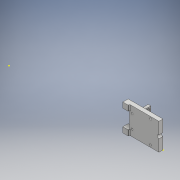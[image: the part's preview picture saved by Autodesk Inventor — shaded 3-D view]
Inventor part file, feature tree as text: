
AUTODESK INVENTOR PART (.ipt)
format: ipt  version: 2018 (Build 220112000, 112)  size: 628,224 bytes
history: native  units: mm
features: sketch x33, extrude x25, fillet x8, hole x6
ambient origin geometry x8: Origin, YZ Plane, XZ Plane, XY Plane, X Axis, Y Axis, Z Axis, Center Point
bodies: Solid1 (feature_tree)
feature tree (72):
  extrude  "Extrusion1"  Depth=50.0mm
  hole  "Hole1"  [1 undecoded]
  hole  "Hole2"  [1 undecoded]
  extrude  "Extrusion2"  Depth=25.0mm
  extrude  "Extrusion3"  Depth=25.0mm
  extrude  "Extrusion4"  Depth=5.0mm
  sketch  "Sketch7"  dims[d25=10.0mm d26=5.0mm]
  extrude  "Extrusion5"  Depth=5.0mm
  extrude  "Extrusion6"  Depth=17.5mm
  extrude  "Extrusion7"  Depth=35.0mm
  extrude  "Extrusion8"  Depth=35.0mm
  extrude  "Extrusion9"  Depth=2.0mm TaperAngle=0.0deg
  extrude  "Extrusion10"  Depth=7.5mm TaperAngle=0.0deg
  extrude  "Extrusion11"  Depth=10.0mm
  extrude  "Extrusion12"  Depth=7.5mm
  fillet  "Fillet1"  Radius=7.5mm
  fillet  "Fillet2"  Radius=25.0mm
  fillet  "Fillet3"  Radius=3.0mm
  fillet  "Fillet4"  Radius=3.2mm
  fillet  "Fillet5"  Radius=2.1mm
  fillet  "Fillet6"  Radius=5.5mm
  extrude  "Extrusion13"  Depth=92.5mm TaperAngle=0.0deg
  sketch  "Sketch17"  dims[d58=4.25mm d59=241.0mm d60=0.0mm]
  hole  "Hole3"  [1 undecoded]
  hole  "Hole4"  [1 undecoded]
  extrude  "Extrusion14"  Depth=5.0mm
  extrude  "Extrusion15"  Depth=2.5mm TaperAngle=0.0deg
  extrude  "Extrusion16"  Depth=30.0mm
  extrude  "Extrusion17"  Depth=2.5mm
  extrude  "Extrusion18"  Depth=14.55mm TaperAngle=0.0deg
  extrude  "Extrusion19"  Depth=0.1mm
  extrude  "Extrusion20"  Depth=3.25mm
  extrude  "Extrusion21"  Depth=3.25mm
  hole  "Hole5"  [1 undecoded]
  extrude  "Extrusion22"  Depth=2.0mm
  extrude  "Extrusion23"  Depth=15.0mm
  extrude  "Extrusion24"  Depth=10.0mm TaperAngle=0.0deg
  extrude  "Extrusion25"  Depth=2.0mm
  fillet  "Fillet7"  Radius=100.0mm
  fillet  "Fillet8"  Radius=100.0mm
  hole  "Hole6"  [1 undecoded]
  sketch  "Sketch1"  dims[d0=50.0mm d1=50.0mm]
  sketch  "Sketch2"  dims[d2=240.0mm d3=7.5mm]
  sketch  "Sketch3"  dims[d4=7.5mm d5=7.5mm d6=0.0mm]
  sketch  "Sketch4"  dims[d7=6.35mm d8=6.0mm d9=4.0mm d10=2.0mm d11=90.0deg d12=8.0mm d13=20.594885mm d14=25.0mm]
  sketch  "Sketch5"  dims[d15=3.3mm d16=6.0mm d17=4.0mm d18=2.0mm d19=90.0deg d20=8.0mm d21=20.594885mm d22=25.0mm]
  sketch  "Sketch6"  dims[d23=180.0deg d24=5.0mm]
  sketch  "Sketch8"  dims[d27=17.5mm d28=0.0mm d30=35.0mm]
  sketch  "Sketch9"  dims[d31=35.0mm d32=35.0mm]
  sketch  "Sketch10"  dims[d33=35.0mm d34=35.0mm]
  sketch  "Sketch11"  dims[d35=35.0mm d36=2.0mm d37=0.0mm]
  sketch  "Sketch12"  dims[d38=10.0mm d39=7.5mm d40=0.0mm]
  sketch  "Sketch13"  dims[d41=100.0mm d42=10.0mm]
  sketch  "Sketch14"  dims[d43=7.5mm d44=0.0mm d45=7.5mm d46=7.5mm d47=25.0mm d48=0.0mm d49=3.0mm d50=3.2mm d51=2.1mm d52=5.5mm]
  sketch  "Sketch15"  dims[d53=3.3mm d54=92.5mm d55=0.0mm]
  sketch  "Sketch16"  dims[d56=5.5mm d57=3.3mm]
  sketch  "Sketch18"  dims[d61=4.44mm d62=5.0mm]
  sketch  "Sketch19"  dims[d63=2.5mm d64=91.25mm d65=0.0mm]
  sketch  "Sketch20"  dims[d66=30.0mm d67=6.35mm]
  sketch  "Sketch21"  dims[d68=3.8mm d69=0.0mm d70=2.5mm]
  sketch  "Sketch22"  dims[d71=14.55mm d72=0.0mm d73=14.55mm d74=0.0mm]
  sketch  "Sketch23"  dims[d75=0.1mm d76=0.1mm]
  sketch  "Sketch24"  dims[d77=3.25mm d78=3.25mm]
  sketch  "Sketch25"  dims[d79=3.25mm d80=3.25mm]
  sketch  "Sketch26"  dims[d81=35.0mm d82=10.0mm]
  sketch  "Sketch27"  dims[d83=2.0mm d84=0.0mm d85=3.6mm]
  sketch  "Sketch28"  dims[d86=3.6mm]
  sketch  "Sketch29"  dims[d87=3.3mm d88=6.0mm d89=4.0mm d90=2.0mm d91=90.0deg d92=15.0mm d93=20.594885mm]
  sketch  "Sketch30"  dims[d94=3.3mm d95=6.0mm d96=4.0mm d97=2.0mm d98=90.0deg d99=15.0mm d100=20.594885mm d101=6.0mm]
  sketch  "Sketch31"  dims[d102=20.0mm d103=0.0mm d104=10.0mm d105=0.0mm]
  sketch  "Sketch32"  dims[d106=2.0mm d107=0.0mm d108=4.0mm d109=100.0mm d110=0.0mm d111=100.0mm d112=0.0mm]
  sketch  "Sketch33"  dims[d113=5.0mm d114=2.0mm d115=0.0mm d116=3.3mm d117=3.3mm d118=3.3mm d119=3.3mm d120=2.0mm d121=0.0mm d122=5.5mm d123=0.0mm d124=3.3mm d125=6.0mm d126=4.0mm d127=2.0mm d128=90.0deg d129=8.0mm d130=20.594885mm d131=42.0mm d132=17.0mm d133=21.0mm d135=8.5mm d136=15.825mm d137=3.5mm d138=21.0mm d139=3.3mm d140=3.3mm d141=3.3mm d142=10.0mm d143=0.0mm d144=7.5mm d145=0.0mm d146=100.0mm d147=0.0mm d148=10.0mm d149=10.0mm d150=10.0mm d151=10.0mm d152=10.0mm d153=0.0mm d154=2.0mm d155=2.0mm d156=6.25mm d157=6.0mm d158=4.0mm d159=2.0mm d160=90.0deg d161=8.0mm d162=0.0mm]
note: 6 required parameter values undecoded (feature->parameter linkage not recoverable at this tier; creation-order binding heuristic only, values carry confidence <= 0.55)
